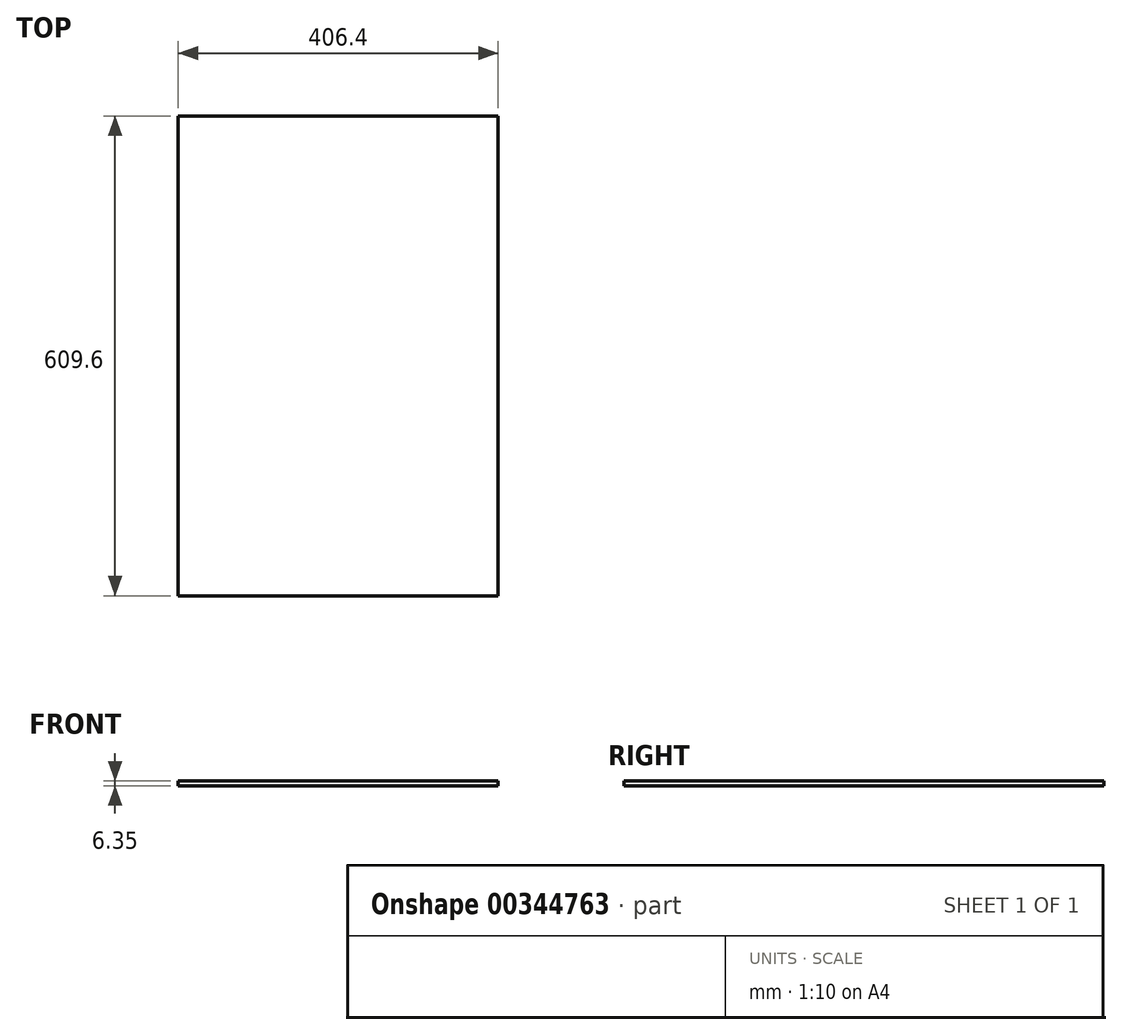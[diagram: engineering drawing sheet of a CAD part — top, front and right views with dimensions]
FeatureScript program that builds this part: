
annotation { "Feature Type Name" : "Feature", "Feature Type Description" : "" }
export const myFeature = defineFeature(function(context is Context, id is Id, definition is map)
    precondition{}
    {
        {
            var Q0;
            Q0=qCreatedBy(makeId("Top.planeOp"),FACE);
            var sketch = newSketch(context, id + "F0", { "sketchPlane" : qUnion([Q0])});
            skLineSegment(sketch, "E0.bottom", {"start": v(0, 0) * mm, "end": v(406.4, 0) * mm});
            skLineSegment(sketch, "E0.top", {"start": v(0, 609.6) * mm, "end": v(406.4, 609.6) * mm});
            skLineSegment(sketch, "E0.left", {"start": v(0, 0) * mm, "end": v(0, 609.6) * mm});
            skLineSegment(sketch, "E0.right", {"start": v(406.4, 0) * mm, "end": v(406.4, 609.6) * mm});
            skSolve(sketch);
        }
        {
            var Q0;
            Q0=makeQuery(id+"F0.imprint","IMPRINT",FACE,{"disambiguationData":[TD([[makeQuery(id+"F0.imprint","IMPRINT",EDGE,{"derivedFrom":sQuery(id+"F0.wireOp",EDGE,"E0.bottom")}),1.0]])]});
            extrude(context, id + "F1", {"entities" : qUnion([Q0]), "depth" : 6.35 * mm});
        }
    });
